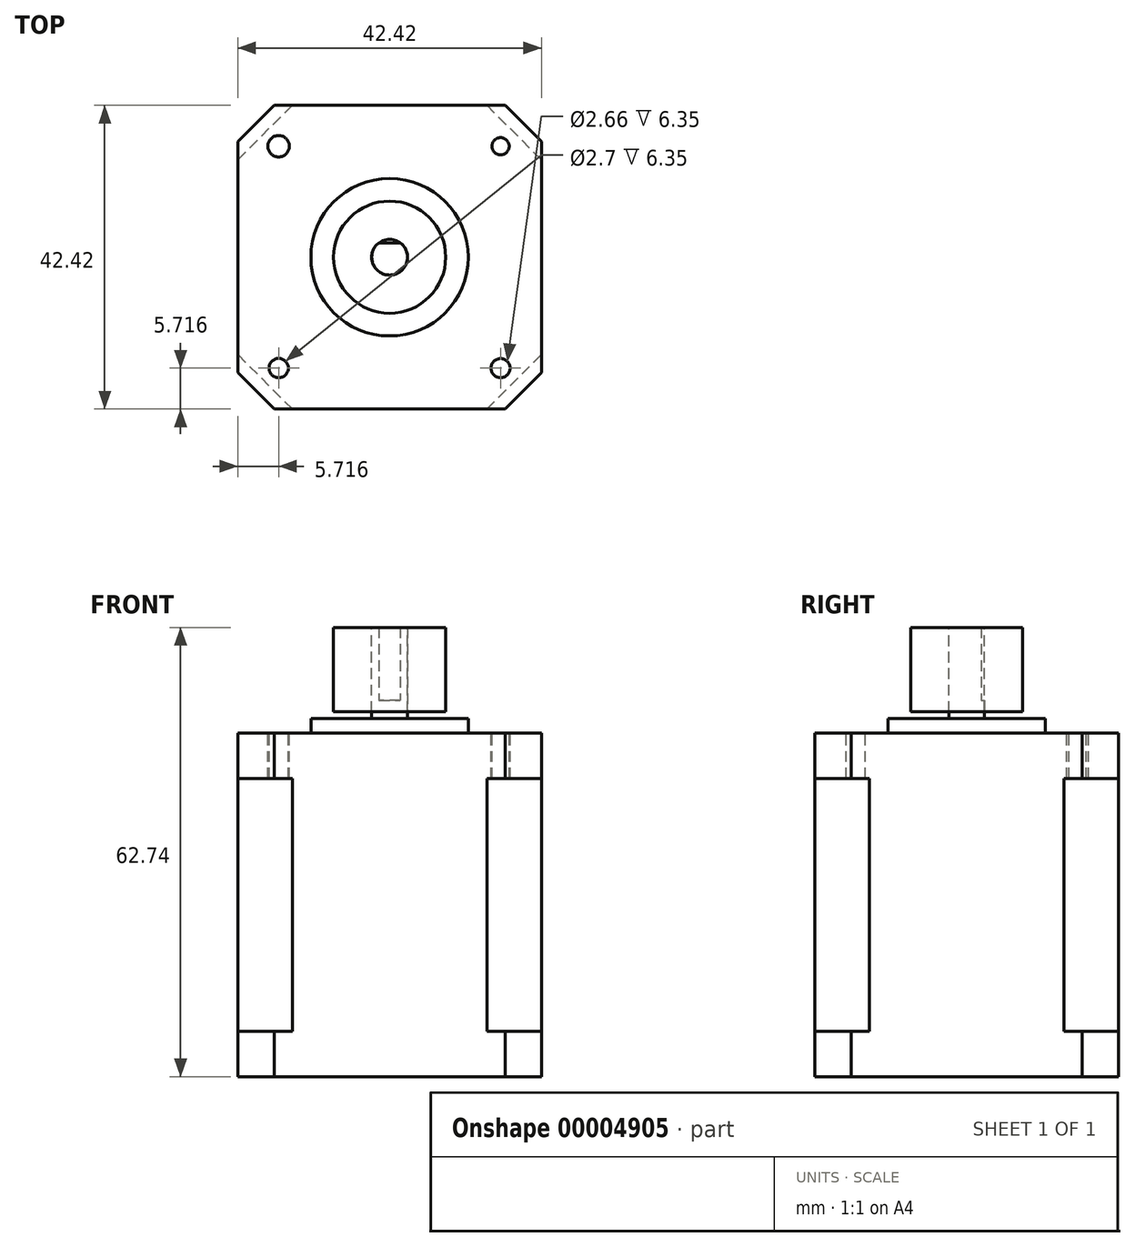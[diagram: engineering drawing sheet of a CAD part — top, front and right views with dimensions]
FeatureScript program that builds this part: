
annotation { "Feature Type Name" : "Feature", "Feature Type Description" : "" }
export const myFeature = defineFeature(function(context is Context, id is Id, definition is map)
    precondition{}
    {
        {
            var Q0;
            Q0=qCreatedBy(makeId("Top.planeOp"),FACE);
            var sketch = newSketch(context, id + "F0", { "sketchPlane" : qUnion([Q0])});
            skLineSegment(sketch, "E0.bottom", {"start": v(-21.2, 21.2) * mm, "end": v(21.2, 21.2) * mm});
            skLineSegment(sketch, "E0.top", {"start": v(-21.2, -21.2) * mm, "end": v(21.2, -21.2) * mm});
            skLineSegment(sketch, "E0.left", {"start": v(-21.2, 21.2) * mm, "end": v(-21.2, -21.2) * mm});
            skLineSegment(sketch, "E0.right", {"start": v(21.2, 21.2) * mm, "end": v(21.2, -21.2) * mm});
            skSolve(sketch);
        }
        {
            var Q0;
            Q0=makeQuery(id+"F0.imprint","IMPRINT",FACE,{"disambiguationData":[TD([[makeQuery(id+"F0.imprint","IMPRINT",EDGE,{"derivedFrom":sQuery(id+"F0.wireOp",EDGE,"E0.bottom")}),-1.0]])]});
            extrude(context, id + "F1", {"entities" : qUnion([Q0]), "endBound" : BoundingType.SYMMETRIC, "depth" : 35.3 * mm});
        }
        {
            var Q0;
            Q0=makeQuery(id+"F1.opExtrude","SWEPT_EDGE",EDGE,{"disambiguationData":[OSD([sQuery(id+"F0.wireOp",EDGE,"E0.bottom"),sQuery(id+"F0.wireOp",EDGE,"E0.right")])]});
            var Q1;
            Q1=makeQuery(id+"F1.opExtrude","SWEPT_EDGE",EDGE,{"disambiguationData":[OSD([sQuery(id+"F0.wireOp",EDGE,"E0.bottom"),sQuery(id+"F0.wireOp",EDGE,"E0.left")])]});
            var Q2;
            Q2=makeQuery(id+"F1.opExtrude","SWEPT_EDGE",EDGE,{"disambiguationData":[OSD([sQuery(id+"F0.wireOp",EDGE,"E0.top"),sQuery(id+"F0.wireOp",EDGE,"E0.left")])]});
            var Q3;
            Q3=makeQuery(id+"F1.opExtrude","SWEPT_EDGE",EDGE,{"disambiguationData":[OSD([sQuery(id+"F0.wireOp",EDGE,"E0.top"),sQuery(id+"F0.wireOp",EDGE,"E0.right")])]});
            chamfer(context, id + "F2", {"entities" : qUnion([Q0, Q1, Q2, Q3]), "width" : 7.62 * mm, "tangentPropagation" : true});
        }
        {
            var Q0;
            Q0=makeQuery(id+"F1.opExtrude","CAP_FACE",FACE,{"disambiguationData":[OSD([sQuery(id+"F0.wireOp",EDGE,"E0.bottom"),sQuery(id+"F0.wireOp",EDGE,"E0.top"),sQuery(id+"F0.wireOp",EDGE,"E0.left"),sQuery(id+"F0.wireOp",EDGE,"E0.right")])],"isStart":false});
            var sketch = newSketch(context, id + "F3", { "sketchPlane" : qUnion([Q0])});
            skLineSegment(sketch, "E1.bottom", {"start": v(-21.2, 21.2) * mm, "end": v(21.2, 21.2) * mm});
            skLineSegment(sketch, "E1.top", {"start": v(-21.2, -21.2) * mm, "end": v(21.2, -21.2) * mm});
            skLineSegment(sketch, "E1.left", {"start": v(-21.2, 21.2) * mm, "end": v(-21.2, -21.2) * mm});
            skLineSegment(sketch, "E1.right", {"start": v(21.2, 21.2) * mm, "end": v(21.2, -21.2) * mm});
            skSolve(sketch);
        }
        {
            var Q0;
            {var subQ0=sQuery(id+"F0.wireOp",EDGE,"E0.top");var subQ1=sQuery(id+"F0.wireOp",EDGE,"E0.right");var subQ2=sQuery(id+"F0.wireOp",EDGE,"E0.bottom");var subQ3=sQuery(id+"F0.wireOp",EDGE,"E0.left");var subQ4=makeQuery(id+"F1.opExtrude","CAP_FACE",FACE,{"disambiguationData":[OSD([subQ2,subQ0,subQ3,subQ1])],"isStart":false});var subQ8=makeQuery(id+"F2.opChamfer","BLEND_EDGE",EDGE,{"blendedFrom":[makeQuery(id+"F1.opExtrude","SWEPT_EDGE",EDGE,{"disambiguationData":[OSD([subQ2,subQ3])]}),subQ4],"blendedInto":[subQ4]});Q0=makeQuery(id+"F3.imprint","IMPRINT",FACE,{"disambiguationData":[TD([[makeQuery(id+"F3.imprint","IMPRINT",EDGE,{"derivedFrom":subQ8}),1.0]])]});}
            var Q1;
            {var subQ0=sQuery(id+"F0.wireOp",EDGE,"E0.bottom");var subQ1=sQuery(id+"F0.wireOp",EDGE,"E0.right");var subQ2=makeQuery(id+"F2.opChamfer","BLEND_EDGE",EDGE,{"blendedFrom":[makeQuery(id+"F1.opExtrude","SWEPT_EDGE",EDGE,{"disambiguationData":[OSD([subQ0,subQ1])]}),makeQuery(id+"F1.opExtrude","CAP_FACE",FACE,{"disambiguationData":[OSD([subQ0,sQuery(id+"F0.wireOp",EDGE,"E0.top"),sQuery(id+"F0.wireOp",EDGE,"E0.left"),subQ1])],"isStart":false})],"blendedInto":[makeQuery(id+"F1.opExtrude","CAP_FACE",FACE,{"disambiguationData":[OSD([subQ0,sQuery(id+"F0.wireOp",EDGE,"E0.top"),sQuery(id+"F0.wireOp",EDGE,"E0.left"),subQ1])],"isStart":false})]});Q1=makeQuery(id+"F3.imprint","IMPRINT",FACE,{"disambiguationData":[TD([[makeQuery(id+"F3.imprint","IMPRINT",EDGE,{"derivedFrom":subQ2}),-1.0]])]});}
            var Q2;
            {var subQ0=sQuery(id+"F0.wireOp",EDGE,"E0.bottom");var subQ1=sQuery(id+"F0.wireOp",EDGE,"E0.left");var subQ2=makeQuery(id+"F2.opChamfer","BLEND_EDGE",EDGE,{"blendedFrom":[makeQuery(id+"F1.opExtrude","SWEPT_EDGE",EDGE,{"disambiguationData":[OSD([subQ0,subQ1])]}),makeQuery(id+"F1.opExtrude","CAP_FACE",FACE,{"disambiguationData":[OSD([subQ0,sQuery(id+"F0.wireOp",EDGE,"E0.top"),subQ1,sQuery(id+"F0.wireOp",EDGE,"E0.right")])],"isStart":false})],"blendedInto":[makeQuery(id+"F1.opExtrude","CAP_FACE",FACE,{"disambiguationData":[OSD([subQ0,sQuery(id+"F0.wireOp",EDGE,"E0.top"),subQ1,sQuery(id+"F0.wireOp",EDGE,"E0.right")])],"isStart":false})]});Q2=makeQuery(id+"F3.imprint","IMPRINT",FACE,{"disambiguationData":[TD([[makeQuery(id+"F3.imprint","IMPRINT",EDGE,{"derivedFrom":subQ2}),-1.0]])]});}
            var Q3;
            {var subQ0=sQuery(id+"F0.wireOp",EDGE,"E0.top");var subQ1=sQuery(id+"F0.wireOp",EDGE,"E0.left");var subQ2=makeQuery(id+"F2.opChamfer","BLEND_EDGE",EDGE,{"blendedFrom":[makeQuery(id+"F1.opExtrude","SWEPT_EDGE",EDGE,{"disambiguationData":[OSD([subQ0,subQ1])]}),makeQuery(id+"F1.opExtrude","CAP_FACE",FACE,{"disambiguationData":[OSD([sQuery(id+"F0.wireOp",EDGE,"E0.bottom"),subQ0,subQ1,sQuery(id+"F0.wireOp",EDGE,"E0.right")])],"isStart":false})],"blendedInto":[makeQuery(id+"F1.opExtrude","CAP_FACE",FACE,{"disambiguationData":[OSD([sQuery(id+"F0.wireOp",EDGE,"E0.bottom"),subQ0,subQ1,sQuery(id+"F0.wireOp",EDGE,"E0.right")])],"isStart":false})]});Q3=makeQuery(id+"F3.imprint","IMPRINT",FACE,{"disambiguationData":[TD([[makeQuery(id+"F3.imprint","IMPRINT",EDGE,{"derivedFrom":subQ2}),-1.0]])]});}
            var Q4;
            {var subQ0=sQuery(id+"F0.wireOp",EDGE,"E0.top");var subQ1=sQuery(id+"F0.wireOp",EDGE,"E0.right");var subQ2=makeQuery(id+"F2.opChamfer","BLEND_EDGE",EDGE,{"blendedFrom":[makeQuery(id+"F1.opExtrude","SWEPT_EDGE",EDGE,{"disambiguationData":[OSD([subQ0,subQ1])]}),makeQuery(id+"F1.opExtrude","CAP_FACE",FACE,{"disambiguationData":[OSD([sQuery(id+"F0.wireOp",EDGE,"E0.bottom"),subQ0,sQuery(id+"F0.wireOp",EDGE,"E0.left"),subQ1])],"isStart":false})],"blendedInto":[makeQuery(id+"F1.opExtrude","CAP_FACE",FACE,{"disambiguationData":[OSD([sQuery(id+"F0.wireOp",EDGE,"E0.bottom"),subQ0,sQuery(id+"F0.wireOp",EDGE,"E0.left"),subQ1])],"isStart":false})]});Q4=makeQuery(id+"F3.imprint","IMPRINT",FACE,{"disambiguationData":[TD([[makeQuery(id+"F3.imprint","IMPRINT",EDGE,{"derivedFrom":subQ2}),-1.0]])]});}
            extrude(context, id + "F4", {"entities" : qUnion([Q0, Q1, Q2, Q3, Q4]), "operationType" : NewBodyOperationType.ADD, "depth" : 6.35 * mm});
        }
        {
            var Q0;
            Q0=makeQuery(id+"F4.opExtrude","SWEPT_EDGE",EDGE,{"disambiguationData":[OSD([sQuery(id+"F3.wireOp",EDGE,"E1.bottom"),sQuery(id+"F3.wireOp",EDGE,"E1.right")])]});
            var Q1;
            Q1=makeQuery(id+"F4.opExtrude","SWEPT_EDGE",EDGE,{"disambiguationData":[OSD([sQuery(id+"F3.wireOp",EDGE,"E1.bottom"),sQuery(id+"F3.wireOp",EDGE,"E1.left")])]});
            var Q2;
            Q2=makeQuery(id+"F4.opExtrude","SWEPT_EDGE",EDGE,{"disambiguationData":[OSD([sQuery(id+"F3.wireOp",EDGE,"E1.top"),sQuery(id+"F3.wireOp",EDGE,"E1.left")])]});
            var Q3;
            Q3=makeQuery(id+"F4.opExtrude","SWEPT_EDGE",EDGE,{"disambiguationData":[OSD([sQuery(id+"F3.wireOp",EDGE,"E1.top"),sQuery(id+"F3.wireOp",EDGE,"E1.right")])]});
            chamfer(context, id + "F5", {"entities" : qUnion([Q0, Q1, Q2, Q3]), "width" : 5.08 * mm, "tangentPropagation" : true});
        }
        {
            var Q0;
            Q0=makeQuery(id+"F1.opExtrude","CAP_FACE",FACE,{"disambiguationData":[OSD([sQuery(id+"F0.wireOp",EDGE,"E0.bottom"),sQuery(id+"F0.wireOp",EDGE,"E0.top"),sQuery(id+"F0.wireOp",EDGE,"E0.left"),sQuery(id+"F0.wireOp",EDGE,"E0.right")])],"isStart":true});
            var sketch = newSketch(context, id + "F6", { "sketchPlane" : qUnion([Q0])});
            skLineSegment(sketch, "E2.0.0", {"start": v(-16.13, 21.2) * mm, "end": v(16.13, 21.2) * mm});
            skLineSegment(sketch, "E2.0.1", {"start": v(16.13, 21.2) * mm, "end": v(21.2, 16.13) * mm});
            skLineSegment(sketch, "E2.0.2", {"start": v(21.2, -16.13) * mm, "end": v(21.2, 16.13) * mm});
            skLineSegment(sketch, "E2.0.3", {"start": v(21.2, -16.13) * mm, "end": v(16.13, -21.2) * mm});
            skLineSegment(sketch, "E2.0.4", {"start": v(-16.13, -21.2) * mm, "end": v(16.13, -21.2) * mm});
            skLineSegment(sketch, "E2.0.5", {"start": v(-16.13, -21.2) * mm, "end": v(-21.2, -16.13) * mm});
            skLineSegment(sketch, "E2.0.6", {"start": v(-21.2, -16.13) * mm, "end": v(-21.2, 16.13) * mm});
            skLineSegment(sketch, "E2.0.7", {"start": v(-21.2, 16.13) * mm, "end": v(-16.13, 21.2) * mm});
            skSolve(sketch);
        }
        {
            var Q0;
            {var subQ3=sQuery(id+"F6.wireOp",EDGE,"E2.0.7");Q0=makeQuery(id+"F6.imprint","IMPRINT",FACE,{"disambiguationData":[TD([[makeQuery(id+"F6.imprint","IMPRINT",EDGE,{"derivedFrom":subQ3}),-1.0]])]});}
            var Q1;
            {var subQ4=sQuery(id+"F6.wireOp",EDGE,"E2.0.1");Q1=makeQuery(id+"F6.imprint","IMPRINT",FACE,{"disambiguationData":[TD([[makeQuery(id+"F6.imprint","IMPRINT",EDGE,{"derivedFrom":subQ4}),-1.0]])]});}
            var Q2;
            {var subQ4=sQuery(id+"F6.wireOp",EDGE,"E2.0.3");Q2=makeQuery(id+"F6.imprint","IMPRINT",FACE,{"disambiguationData":[TD([[makeQuery(id+"F6.imprint","IMPRINT",EDGE,{"derivedFrom":subQ4}),-1.0]])]});}
            var Q3;
            {var subQ4=sQuery(id+"F6.wireOp",EDGE,"E2.0.5");Q3=makeQuery(id+"F6.imprint","IMPRINT",FACE,{"disambiguationData":[TD([[makeQuery(id+"F6.imprint","IMPRINT",EDGE,{"derivedFrom":subQ4}),-1.0]])]});}
            var Q4;
            {var subQ0=sQuery(id+"F0.wireOp",EDGE,"E0.top");var subQ1=sQuery(id+"F0.wireOp",EDGE,"E0.right");var subQ2=sQuery(id+"F0.wireOp",EDGE,"E0.bottom");var subQ3=sQuery(id+"F0.wireOp",EDGE,"E0.left");var subQ4=makeQuery(id+"F1.opExtrude","CAP_FACE",FACE,{"disambiguationData":[OSD([subQ2,subQ0,subQ3,subQ1])],"isStart":true});var subQ8=makeQuery(id+"F2.opChamfer","BLEND_EDGE",EDGE,{"blendedFrom":[makeQuery(id+"F1.opExtrude","SWEPT_EDGE",EDGE,{"disambiguationData":[OSD([subQ2,subQ3])]}),subQ4],"blendedInto":[subQ4]});Q4=makeQuery(id+"F6.imprint","IMPRINT",FACE,{"disambiguationData":[TD([[makeQuery(id+"F6.imprint","IMPRINT",EDGE,{"derivedFrom":subQ8}),1.0]])]});}
            extrude(context, id + "F7", {"entities" : qUnion([Q0, Q1, Q2, Q3, Q4]), "operationType" : NewBodyOperationType.ADD, "depth" : 6.35 * mm});
        }
        {
            var Q0;
            Q0=makeQuery(id+"F4.opExtrude","CAP_FACE",FACE,{"disambiguationData":[OSD([sQuery(id+"F3.wireOp",EDGE,"E1.bottom"),sQuery(id+"F3.wireOp",EDGE,"E1.top"),sQuery(id+"F3.wireOp",EDGE,"E1.left"),sQuery(id+"F3.wireOp",EDGE,"E1.right")])],"isStart":false});
            var sketch = newSketch(context, id + "F8", { "sketchPlane" : qUnion([Q0])});
            skCircle(sketch, "E3", {"center": v(0, 0) * mm, "radius": 11 * mm});
            skSolve(sketch);
        }
        {
            var Q0;
            Q0=makeQuery(id+"F8.imprint","IMPRINT",FACE,{"disambiguationData":[TD([[makeQuery(id+"F8.imprint","IMPRINT",EDGE,{"derivedFrom":sQuery(id+"F8.wireOp",EDGE,"E3")}),1.0]])]});
            extrude(context, id + "F9", {"entities" : qUnion([Q0]), "operationType" : NewBodyOperationType.ADD, "depth" : 2.03 * mm});
        }
        {
            var Q0;
            Q0=makeQuery(id+"F9.opExtrude","CAP_FACE",FACE,{"disambiguationData":[OSD([sQuery(id+"F8.wireOp",EDGE,"E3")])],"isStart":false});
            var sketch = newSketch(context, id + "F10", { "sketchPlane" : qUnion([Q0])});
            skCircle(sketch, "E4", {"center": v(0, 0) * mm, "radius": 2.5 * mm});
            skSolve(sketch);
        }
        {
            var Q0;
            Q0=makeQuery(id+"F10.imprint","IMPRINT",FACE,{"disambiguationData":[TD([[makeQuery(id+"F10.imprint","IMPRINT",EDGE,{"derivedFrom":sQuery(id+"F10.wireOp",EDGE,"E4")}),1.0]])]});
            extrude(context, id + "F11", {"entities" : qUnion([Q0]), "operationType" : NewBodyOperationType.ADD, "depth" : 12.7 * mm});
        }
        {
            var Q0;
            Q0=makeQuery(id+"F11.opExtrude","CAP_FACE",FACE,{"disambiguationData":[OSD([sQuery(id+"F10.wireOp",EDGE,"E4")])],"isStart":false});
            var sketch = newSketch(context, id + "F12", { "sketchPlane" : qUnion([Q0])});
            skLineSegment(sketch, "E5.bottom", {"start": v(-2.63, 2.93) * mm, "end": v(2.62, 2.93) * mm});
            skLineSegment(sketch, "E5.top", {"start": v(-2.63, 2) * mm, "end": v(2.62, 2) * mm});
            skLineSegment(sketch, "E5.left", {"start": v(-2.63, 2.93) * mm, "end": v(-2.63, 2) * mm});
            skLineSegment(sketch, "E5.right", {"start": v(2.62, 2.93) * mm, "end": v(2.62, 2) * mm});
            skSolve(sketch);
        }
        {
            var Q0;
            {var subQ0=makeQuery(id+"F11.opExtrude","CAP_EDGE",EDGE,{"disambiguationData":[OSD([sQuery(id+"F10.wireOp",EDGE,"E4")])],"isStart":false});var subQ1=sQuery(id+"F12.wireOp",EDGE,"E5.top");var subQ3=makeQuery(id+"F12.imprint","INTERSECT",VERTEX,{"disambiguationData":[OD(0.0)],"derivedFrom":[subQ0,subQ1]});Q0=qUnion([makeQuery(id+"F12.imprint","IMPRINT",FACE,{"disambiguationData":[TD([[makeQuery(id+"F12.imprint","IMPRINT",EDGE,{"derivedFrom":sQuery(id+"F12.wireOp",EDGE,"E5.bottom")}),-1.0]])]}),makeQuery(id+"F12.imprint","IMPRINT",FACE,{"disambiguationData":[TD([[makeQuery(id+"F12.imprint","IMPRINT",EDGE,{"disambiguationData":[TD([[subQ3,-1.0]])],"derivedFrom":subQ1}),1.0]])]})]);}
            extrude(context, id + "F13", {"entities" : qUnion([Q0]), "operationType" : NewBodyOperationType.REMOVE, "oppositeDirection" : true, "depth" : 10.16 * mm});
        }
        {
            var Q0;
            Q0=makeQuery(id+"F4.opExtrude","CAP_FACE",FACE,{"disambiguationData":[OSD([sQuery(id+"F3.wireOp",EDGE,"E1.bottom"),sQuery(id+"F3.wireOp",EDGE,"E1.top"),sQuery(id+"F3.wireOp",EDGE,"E1.left"),sQuery(id+"F3.wireOp",EDGE,"E1.right")])],"isStart":false});
            var sketch = newSketch(context, id + "F14", { "sketchPlane" : qUnion([Q0])});
            skCircle(sketch, "E6", {"center": v(-15.5, 15.5) * mm, "radius": 1.5 * mm});
            skCircle(sketch, "E7", {"center": v(15.5, 15.5) * mm, "radius": 1.2 * mm});
            skCircle(sketch, "E8", {"center": v(15.5, -15.5) * mm, "radius": 1.33 * mm});
            skCircle(sketch, "E9", {"center": v(-15.5, -15.5) * mm, "radius": 1.35 * mm});
            skSolve(sketch);
        }
        {
            var Q0;
            {Q0=qUnion([makeQuery(id+"F14.imprint","IMPRINT",FACE,{"disambiguationData":[TD([[makeQuery(id+"F14.imprint","IMPRINT",EDGE,{"derivedFrom":sQuery(id+"F14.wireOp",EDGE,"E6")}),1.0]])]}),makeQuery(id+"F14.imprint","IMPRINT",FACE,{"disambiguationData":[TD([[makeQuery(id+"F14.imprint","IMPRINT",EDGE,{"derivedFrom":sQuery(id+"F14.wireOp",EDGE,"E7")}),1.0]])]}),makeQuery(id+"F14.imprint","IMPRINT",FACE,{"disambiguationData":[TD([[makeQuery(id+"F14.imprint","IMPRINT",EDGE,{"derivedFrom":sQuery(id+"F14.wireOp",EDGE,"E8")}),1.0]])]}),makeQuery(id+"F14.imprint","IMPRINT",FACE,{"disambiguationData":[TD([[makeQuery(id+"F14.imprint","IMPRINT",EDGE,{"derivedFrom":sQuery(id+"F14.wireOp",EDGE,"E9")}),1.0]])]})]);}
            extrude(context, id + "F15", {"entities" : qUnion([Q0]), "operationType" : NewBodyOperationType.REMOVE, "oppositeDirection" : true, "depth" : 6.35 * mm});
        }
        {
            var Q0;
            Q0=makeQuery(id+"F11.opExtrude","CAP_FACE",FACE,{"disambiguationData":[OSD([sQuery(id+"F10.wireOp",EDGE,"E4")])],"isStart":false});
            var sketch = newSketch(context, id + "F16", { "sketchPlane" : qUnion([Q0])});
            skCircle(sketch, "E10", {"center": v(0, 0) * mm, "radius": 7.83 * mm});
            skCircle(sketch, "E11", {"center": v(0, 0) * mm, "radius": 2.5 * mm});
            skSolve(sketch);
        }
        {
            var Q0;
            Q0=makeQuery(id+"F16.imprint","IMPRINT",FACE,{"disambiguationData":[TD([[makeQuery(id+"F16.imprint","IMPRINT",EDGE,{"derivedFrom":sQuery(id+"F16.wireOp",EDGE,"E10")}),1.0]])]});
            extrude(context, id + "F17", {"entities" : qUnion([Q0]), "oppositeDirection" : true, "depth" : 11.8 * mm});
        }
    });
